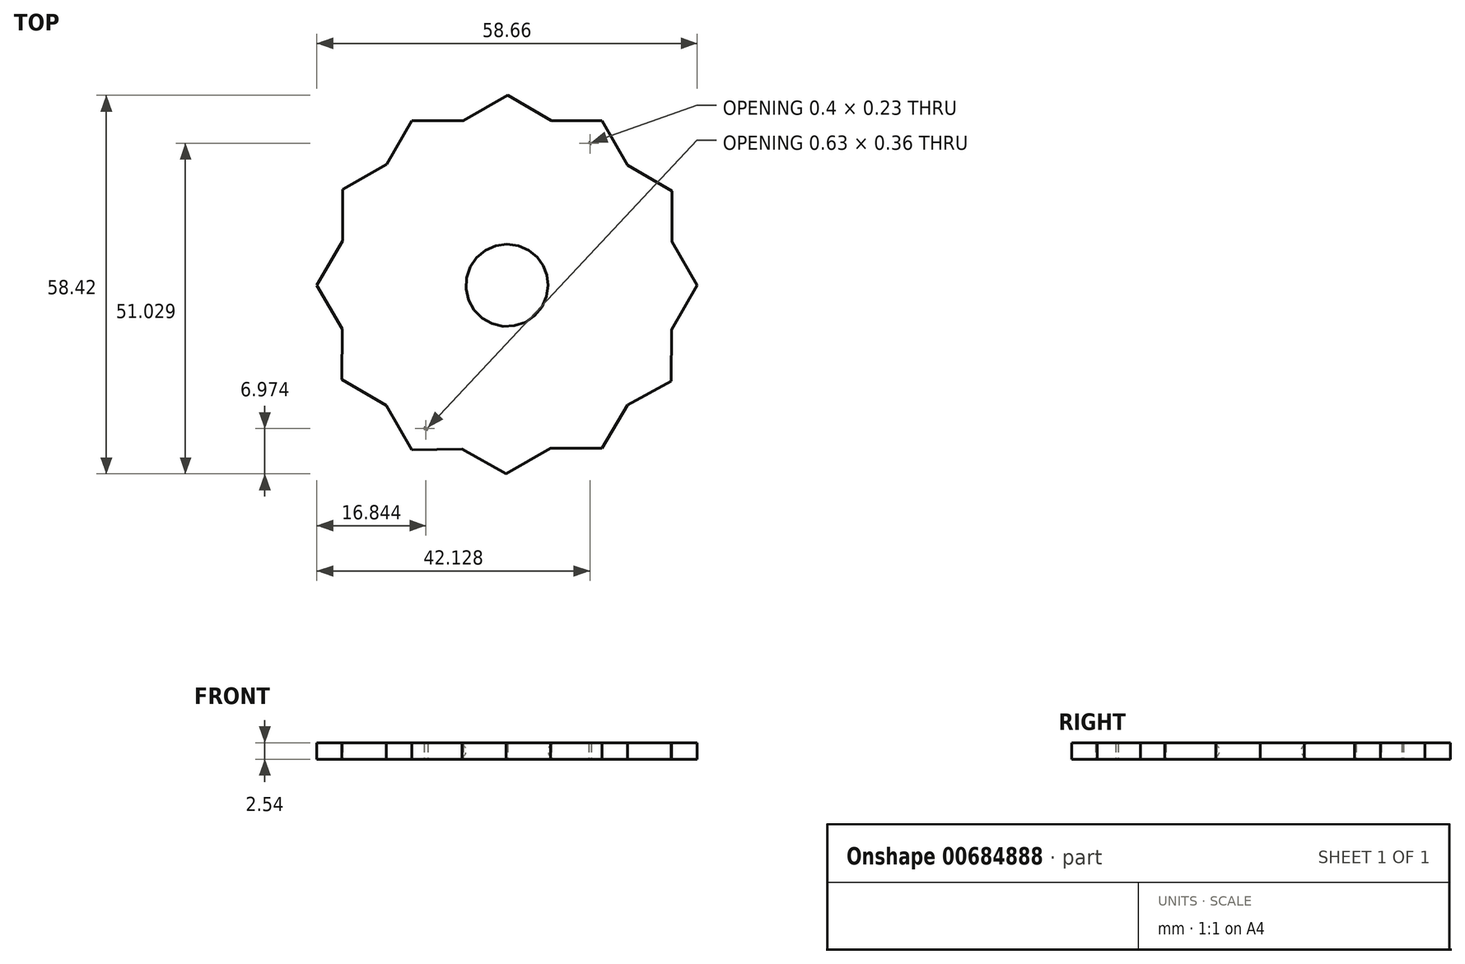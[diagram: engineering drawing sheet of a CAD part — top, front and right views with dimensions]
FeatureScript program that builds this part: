
annotation { "Feature Type Name" : "Feature", "Feature Type Description" : "" }
export const myFeature = defineFeature(function(context is Context, id is Id, definition is map)
    precondition{}
    {
        {
            var Q0;
            Q0=qCreatedBy(makeId("Top.planeOp"),FACE);
            var sketch = newSketch(context, id + "F0", { "sketchPlane" : qUnion([Q0])});
            skCircle(sketch, "E0", {"center": v(0, 0) * mm, "radius": 25.4 * mm});
            skCircle(sketch, "E1.cCircle", {"center": v(0, 0) * mm, "radius": 25.4 * mm, "construction": true});
            skLineSegment(sketch, "E1.1", {"start": v(0.13, 29.33) * mm, "end": v(25.47, 14.55) * mm});
            skLineSegment(sketch, "E1.2", {"start": v(25.47, 14.55) * mm, "end": v(25.33, -14.78) * mm});
            skPoint(sketch, "E1.0.midPoint", {"position": v(-12.6, 22.05) * mm});
            skLineSegment(sketch, "E2", {"start": v(-12.6, 22.05) * mm, "end": v(0.13, 29.33) * mm});
            skLineSegment(sketch, "E3", {"start": v(12.6, 22.05) * mm, "end": v(0.13, 29.33) * mm});
            skLineSegment(sketch, "E4", {"start": v(12.6, 22.05) * mm, "end": v(25.47, 14.55) * mm});
            skLineSegment(sketch, "E5", {"start": v(25.47, 14.55) * mm, "end": v(25.4, 0) * mm});
            skLineSegment(sketch, "E6", {"start": v(25.4, 0) * mm, "end": v(25.33, -14.78) * mm});
            skLineSegment(sketch, "E7", {"start": v(25.33, -14.78) * mm, "end": v(12.6, -21.82) * mm});
            skLineSegment(sketch, "E8", {"start": v(12.6, -21.82) * mm, "end": v(-0.13, -29.1) * mm});
            skLineSegment(sketch, "E9", {"start": v(-12.8, -21.94) * mm, "end": v(-25.47, -14.55) * mm});
            skLineSegment(sketch, "E10", {"start": v(-12.8, -21.94) * mm, "end": v(-0.13, -29.1) * mm});
            skLineSegment(sketch, "E11", {"start": v(-25.33, 14.78) * mm, "end": v(-12.6, 22.05) * mm});
            skLineSegment(sketch, "E12", {"start": v(-25.47, -14.55) * mm, "end": v(-25.4, 0) * mm});
            skLineSegment(sketch, "E13", {"start": v(-25.33, 14.78) * mm, "end": v(-25.4, 0) * mm});
            skLineSegment(sketch, "E14.4", {"start": v(-14.66, -25.4) * mm, "end": v(-29.33, 0) * mm});
            skPoint(sketch, "E14.0.midPoint", {"position": v(0, 25.4) * mm});
            skLineSegment(sketch, "E15", {"start": v(-14.66, 25.4) * mm, "end": v(-18.7, 18.42) * mm});
            skPoint(sketch, "E15.endSnap0", {"position": v(-18.97, 18.42) * mm});
            skLineSegment(sketch, "E16", {"start": v(-14.66, 25.4) * mm, "end": v(-6.74, 25.4) * mm});
            skLineSegment(sketch, "E17", {"start": v(14.66, 25.4) * mm, "end": v(6.87, 25.4) * mm});
            skLineSegment(sketch, "E18", {"start": v(14.66, 25.4) * mm, "end": v(18.63, 18.54) * mm});
            skLineSegment(sketch, "E19", {"start": v(29.33, 0) * mm, "end": v(25.43, 6.75) * mm});
            skLineSegment(sketch, "E20", {"start": v(29.33, 0) * mm, "end": v(25.37, -6.86) * mm});
            skLineSegment(sketch, "E21", {"start": v(14.67, -25.16) * mm, "end": v(18.61, -18.5) * mm});
            skLineSegment(sketch, "E22", {"start": v(14.67, -25.16) * mm, "end": v(6.74, -25.16) * mm});
            skLineSegment(sketch, "E23", {"start": v(-14.66, -25.4) * mm, "end": v(-6.92, -25.26) * mm});
            skLineSegment(sketch, "E24", {"start": v(-14.66, -25.4) * mm, "end": v(-18.63, -18.54) * mm});
            skLineSegment(sketch, "E25", {"start": v(-29.33, 0) * mm, "end": v(-25.43, -6.75) * mm});
            skLineSegment(sketch, "E26", {"start": v(-29.33, 0) * mm, "end": v(-25.37, 6.86) * mm});
            skCircle(sketch, "E27", {"center": v(0, 0) * mm, "radius": 6.35 * mm});
            skSolve(sketch);
        }
        {
            var Q0;
            Q0 = qSketchRegion(id + "F0", true);
            var Q1;
            Q1=makeQuery(id+"F0.imprint","IMPRINT",FACE,{"disambiguationData":[TD([[makeQuery(id+"F0.imprint","IMPRINT",EDGE,{"derivedFrom":sQuery(id+"F0.wireOp",EDGE,"E27")}),-1.0]])]});
            var Q2;
            {var subQ0=sQuery(id+"F0.wireOp",EDGE,"E8");var subQ1=sQuery(id+"F0.wireOp",EDGE,"E0");var subQ2=makeQuery(id+"F0.imprint","INTERSECT",VERTEX,{"derivedFrom":[subQ1,subQ0]});Q2=makeQuery(id+"F0.imprint","IMPRINT",FACE,{"disambiguationData":[TD([[makeQuery(id+"F0.imprint","IMPRINT",EDGE,{"disambiguationData":[TD([[subQ2,-1.0]])],"derivedFrom":subQ1}),1.0]])]});}
            extrude(context, id + "F1", {"entities" : qUnion([Q0, Q1, Q2]), "depth" : 2.54 * mm, "offsetDistance" : 25.4 * mm});
        }
        {
            var Q0;
            Q0=makeQuery(id+"F1.opExtrude","CAP_EDGE",EDGE,{"disambiguationData":[OSD([sQuery(id+"F0.wireOp",EDGE,"E27")])],"isStart":false});
            var Q1;
            Q1=makeQuery(id+"F1.opExtrude","CAP_EDGE",EDGE,{"disambiguationData":[OSD([sQuery(id+"F0.wireOp",EDGE,"E27")])],"isStart":true});
            fillet(context, id + "F2", {"entities" : qUnion([Q0, Q1]), "radius" : 1.27 * mm, "tangentPropagation" : true, "allowEdgeOverflow" : false});
        }
    });
